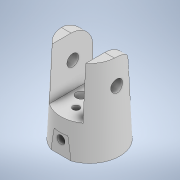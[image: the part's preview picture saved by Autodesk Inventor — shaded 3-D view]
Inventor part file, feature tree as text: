
AUTODESK INVENTOR PART (.ipt)
format: ipt  version: 2021 (Build 250183000, 183)  size: 660,480 bytes
history: native  units: mm
features: sketch x9, other x8, extrude x8, plane x3, fillet x1
ambient origin geometry x8: Origin, YZ Plane, XZ Plane, XY Plane, X Axis, Y Axis, Z Axis, Center Point
bodies: Volumenkörper1 (feature_tree), Volumenkörper5 (feature_tree), Volumenkörper7 (feature_tree), Volumenkörper8 (feature_tree), Volumenkörper9 (feature_tree), Volumenkörper10 (feature_tree)
feature tree (29):
  other  "Fingerteil_3_Daumen"
  extrude  "Extrusion1"  Depth=25.0mm TaperAngle=0.0deg
  other  "Flächenverjüngung1"
  extrude  "Extrusion2"  Depth=10.0mm
  extrude  "Extrusion3"  Depth=3.5mm
  extrude  "Extrusion9"  Depth=30.0mm TaperAngle=0.0deg
  fillet  "Rundung3"  Radius=6.5mm
  other  "Kombinieren2"
  extrude  "Extrusion10"  Depth=6.0mm
  other  "Kombinieren4"
  extrude  "Extrusion11"  Depth=8.5mm TaperAngle=0.0deg
  other  "Kombinieren5"
  plane  "Arbeitsebene1"
  extrude  "Extrusion12"  Depth=6.0mm
  other  "Kombinieren6"
  extrude  "Extrusion13"  Depth=2.0mm
  other  "Kombinieren7"
  plane  "Arbeitsebene2"
  plane  "Arbeitsebene3"
  other  "Prägen2"
  sketch  "Skizze1"  dims[d6=18.0mm d7=25.0mm d8=0.0mm]
  sketch  "Skizze2"  dims[d12=15.0mm d13=0.0mm d14=10.0mm]
  sketch  "Skizze3"  dims[d15=5.0mm d16=3.5mm]
  sketch  "Skizze5"  dims[d18=30.0mm d19=0.0mm d42=30.0mm d43=0.0mm d44=6.5mm]
  sketch  "Skizze7"  dims[d46=7.25mm d47=6.0mm]
  sketch  "Skizze8"  dims[d48=8.5mm d49=40.0mm d50=0.0mm]
  sketch  "Skizze9"  dims[d51=-0.436332mm d52=6.0mm]
  sketch  "Skizze11"  dims[d53=0.0mm d55=2.0mm]
  sketch  "Skizze13"  dims[d56=22.25mm d57=0.0mm d58=5.5mm d60=2.4mm d61=4.0mm d63=22.25mm d64=0.0mm d66=0.0mm d68=15.0mm d69=0.0mm d70=3.0mm d71=3.0mm d72=2.5mm d73=0.0mm d74=2.5mm d75=0.0mm d76=4.0mm d77=9.0mm d84=-9.0mm d85=3.5mm d86=3.5mm d87=3.0mm d88=4.0mm d89=0.5mm d90=0.0mm d17=0.872665mm d37=0.5mm d38=0.872665mm d39=0.5mm d40=0.872665mm d59=0.872665mm d78=0.872665mm d79=0.5mm d80=0.872665mm d91=0.5mm d92=0.872665mm d93=0.5mm d94=0.872665mm]
